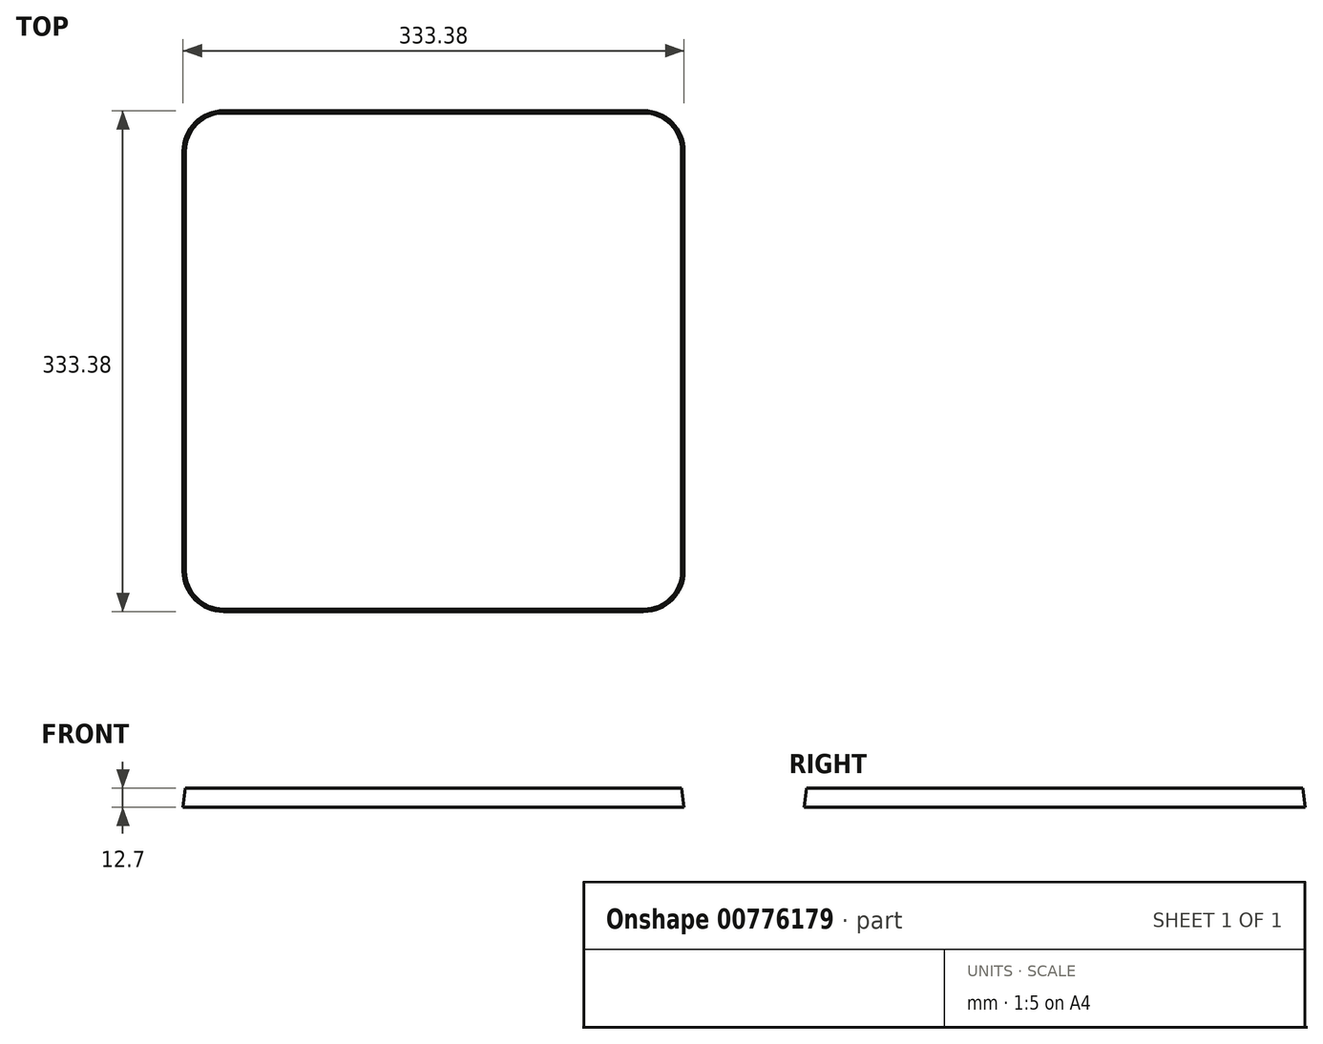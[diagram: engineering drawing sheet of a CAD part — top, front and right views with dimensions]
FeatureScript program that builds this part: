
annotation { "Feature Type Name" : "Feature", "Feature Type Description" : "" }
export const myFeature = defineFeature(function(context is Context, id is Id, definition is map)
    precondition{}
    {
        {
            var Q0;
            Q0=qCreatedBy(makeId("Top.planeOp"),FACE);
            var sketch = newSketch(context, id + "F0", { "sketchPlane" : qUnion([Q0])});
            skLineSegment(sketch, "E0.bottom", {"start": v(139.7, -165.1) * mm, "end": v(-139.7, -165.1) * mm});
            skLineSegment(sketch, "E0.top", {"start": v(139.7, 165.1) * mm, "end": v(-139.7, 165.1) * mm});
            skLineSegment(sketch, "E0.left", {"start": v(165.1, -139.7) * mm, "end": v(165.1, 139.7) * mm});
            skLineSegment(sketch, "E0.right", {"start": v(-165.1, -139.7) * mm, "end": v(-165.1, 139.7) * mm});
            skPoint(sketch, "E0.middle", {"position": v(0, 0) * mm});
            skLineSegment(sketch, "E1.bottom", {"start": v(139.7, -152.4) * mm, "end": v(19.05, -152.4) * mm});
            skLineSegment(sketch, "E1.top", {"start": v(139.7, 152.4) * mm, "end": v(19.05, 152.4) * mm});
            skLineSegment(sketch, "E1.left", {"start": v(152.4, -139.7) * mm, "end": v(152.4, -19.06) * mm});
            skLineSegment(sketch, "E1.right", {"start": v(-152.4, -139.7) * mm, "end": v(-152.4, -19.06) * mm});
            skLineSegment(sketch, "E2.bottom", {"start": v(139.7, -6.36) * mm, "end": v(19.05, -6.36) * mm});
            skLineSegment(sketch, "E2.top", {"start": v(139.7, 6.36) * mm, "end": v(19.05, 6.36) * mm});
            skLineSegment(sketch, "E3.left", {"start": v(6.35, -139.7) * mm, "end": v(6.35, -19.06) * mm});
            skLineSegment(sketch, "E3.right", {"start": v(-6.35, -139.7) * mm, "end": v(-6.35, -19.06) * mm});
            skPoint(sketch, "E4.visualSharp", {"position": v(-165.1, 165.1) * mm});
            skArc(sketch, "E4.filletArc", {"start": v(-139.7, 165.1) * mm, "mid": v(-157.66, 157.66) * mm, "end": v(-165.1, 139.7) * mm});
            skPoint(sketch, "E5.visualSharp", {"position": v(165.1, 165.1) * mm});
            skArc(sketch, "E5.filletArc", {"start": v(165.1, 139.7) * mm, "mid": v(157.66, 157.66) * mm, "end": v(139.7, 165.1) * mm});
            skPoint(sketch, "E6.visualSharp", {"position": v(165.1, -165.1) * mm});
            skArc(sketch, "E6.filletArc", {"start": v(139.7, -165.1) * mm, "mid": v(157.66, -157.66) * mm, "end": v(165.1, -139.7) * mm});
            skPoint(sketch, "E7.visualSharp", {"position": v(-165.1, -165.1) * mm});
            skArc(sketch, "E7.filletArc", {"start": v(-165.1, -139.7) * mm, "mid": v(-157.66, -157.66) * mm, "end": v(-139.7, -165.1) * mm});
            skPoint(sketch, "E8.visualSharp", {"position": v(-152.4, -152.4) * mm});
            skArc(sketch, "E8.filletArc", {"start": v(-152.4, -139.7) * mm, "mid": v(-148.68, -148.68) * mm, "end": v(-139.7, -152.4) * mm});
            skPoint(sketch, "E9.visualSharp", {"position": v(152.4, -152.4) * mm});
            skArc(sketch, "E9.filletArc", {"start": v(139.7, -152.4) * mm, "mid": v(148.68, -148.68) * mm, "end": v(152.4, -139.7) * mm});
            skPoint(sketch, "E10.visualSharp", {"position": v(-152.4, 152.4) * mm});
            skArc(sketch, "E10.filletArc", {"start": v(-139.7, 152.4) * mm, "mid": v(-148.68, 148.68) * mm, "end": v(-152.4, 139.7) * mm});
            skPoint(sketch, "E11.visualSharp", {"position": v(152.4, 152.4) * mm});
            skArc(sketch, "E11.filletArc", {"start": v(152.4, 139.7) * mm, "mid": v(148.68, 148.68) * mm, "end": v(139.7, 152.4) * mm});
            skLineSegment(sketch, "E12.trimOffspring", {"start": v(-6.35, 19.06) * mm, "end": v(-6.35, 139.7) * mm});
            skLineSegment(sketch, "E13.trimOffspring", {"start": v(-19.05, 6.36) * mm, "end": v(-139.7, 6.36) * mm});
            skLineSegment(sketch, "E14.trimOffspring", {"start": v(6.35, 19.06) * mm, "end": v(6.35, 139.7) * mm});
            skLineSegment(sketch, "E15.trimOffspring", {"start": v(-19.05, -6.36) * mm, "end": v(-139.7, -6.36) * mm});
            skLineSegment(sketch, "E16.trimOffspring", {"start": v(-152.4, 19.06) * mm, "end": v(-152.4, 139.7) * mm});
            skLineSegment(sketch, "E17.trimOffspring", {"start": v(-19.05, -152.4) * mm, "end": v(-139.7, -152.4) * mm});
            skLineSegment(sketch, "E18.trimOffspring", {"start": v(152.4, 19.06) * mm, "end": v(152.4, 139.7) * mm});
            skLineSegment(sketch, "E19.trimOffspring", {"start": v(-19.05, 152.4) * mm, "end": v(-139.7, 152.4) * mm});
            skPoint(sketch, "E20.visualSharp", {"position": v(-6.35, 152.4) * mm});
            skArc(sketch, "E20.filletArc", {"start": v(-6.35, 139.7) * mm, "mid": v(-10.06, 148.68) * mm, "end": v(-19.05, 152.4) * mm});
            skPoint(sketch, "E21.visualSharp", {"position": v(6.35, 152.4) * mm});
            skArc(sketch, "E21.filletArc", {"start": v(19.05, 152.4) * mm, "mid": v(10.06, 148.68) * mm, "end": v(6.35, 139.7) * mm});
            skPoint(sketch, "E22.visualSharp", {"position": v(-6.35, 6.36) * mm});
            skArc(sketch, "E22.filletArc", {"start": v(-19.05, 6.36) * mm, "mid": v(-10.06, 10.08) * mm, "end": v(-6.35, 19.06) * mm});
            skPoint(sketch, "E23.visualSharp", {"position": v(-152.4, 6.36) * mm});
            skArc(sketch, "E23.filletArc", {"start": v(-152.4, 19.06) * mm, "mid": v(-148.68, 10.08) * mm, "end": v(-139.7, 6.36) * mm});
            skPoint(sketch, "E24.visualSharp", {"position": v(-152.4, -6.36) * mm});
            skArc(sketch, "E24.filletArc", {"start": v(-139.7, -6.36) * mm, "mid": v(-148.68, -10.08) * mm, "end": v(-152.4, -19.06) * mm});
            skPoint(sketch, "E25.visualSharp", {"position": v(-6.35, -6.36) * mm});
            skArc(sketch, "E25.filletArc", {"start": v(-6.35, -19.06) * mm, "mid": v(-10.06, -10.08) * mm, "end": v(-19.05, -6.36) * mm});
            skPoint(sketch, "E26.visualSharp", {"position": v(6.35, -6.36) * mm});
            skArc(sketch, "E26.filletArc", {"start": v(19.05, -6.36) * mm, "mid": v(10.06, -10.08) * mm, "end": v(6.35, -19.06) * mm});
            skPoint(sketch, "E27.visualSharp", {"position": v(6.35, 6.36) * mm});
            skArc(sketch, "E27.filletArc", {"start": v(6.35, 19.06) * mm, "mid": v(10.06, 10.08) * mm, "end": v(19.05, 6.36) * mm});
            skPoint(sketch, "E28.visualSharp", {"position": v(-6.35, -152.4) * mm});
            skArc(sketch, "E28.filletArc", {"start": v(-19.05, -152.4) * mm, "mid": v(-10.06, -148.68) * mm, "end": v(-6.35, -139.7) * mm});
            skPoint(sketch, "E29.visualSharp", {"position": v(6.35, -152.4) * mm});
            skArc(sketch, "E29.filletArc", {"start": v(6.35, -139.7) * mm, "mid": v(10.06, -148.68) * mm, "end": v(19.05, -152.4) * mm});
            skPoint(sketch, "E30.visualSharp", {"position": v(152.4, -6.36) * mm});
            skArc(sketch, "E30.filletArc", {"start": v(152.4, -19.06) * mm, "mid": v(148.68, -10.08) * mm, "end": v(139.7, -6.36) * mm});
            skPoint(sketch, "E31.visualSharp", {"position": v(152.4, 6.36) * mm});
            skArc(sketch, "E31.filletArc", {"start": v(139.7, 6.36) * mm, "mid": v(148.68, 10.08) * mm, "end": v(152.4, 19.06) * mm});
            skSolve(sketch);
        }
        {
            var Q0;
            Q0=qCreatedBy(makeId("Top.planeOp"),FACE);
            cPlane(context, id + "F1", {"entities" : qUnion([Q0]), "cplaneType" : CPlaneType.OFFSET, "offset" : 190.5 * mm, "width" : 152.4 * mm, "height" : 152.4 * mm});
        }
        {
            var Q0;
            Q0=makeQuery(id+"F0.imprint","IMPRINT",FACE,{"disambiguationData":[TD([[makeQuery(id+"F0.imprint","IMPRINT",EDGE,{"derivedFrom":sQuery(id+"F0.wireOp",EDGE,"E1.bottom")}),-1.0]])]});
            var Q1;
            Q1=makeQuery(id+"F0.imprint","IMPRINT",FACE,{"disambiguationData":[TD([[makeQuery(id+"F0.imprint","IMPRINT",EDGE,{"derivedFrom":sQuery(id+"F0.wireOp",EDGE,"E1.top")}),1.0]])]});
            var Q2;
            Q2=makeQuery(id+"F0.imprint","IMPRINT",FACE,{"disambiguationData":[TD([[makeQuery(id+"F0.imprint","IMPRINT",EDGE,{"derivedFrom":sQuery(id+"F0.wireOp",EDGE,"E1.right")}),-1.0]])]});
            var Q3;
            Q3=makeQuery(id+"F0.imprint","IMPRINT",FACE,{"disambiguationData":[TD([[makeQuery(id+"F0.imprint","IMPRINT",EDGE,{"derivedFrom":sQuery(id+"F0.wireOp",EDGE,"E10.filletArc")}),1.0]])]});
            var Q4;
            Q4=makeQuery(id+"F0.imprint","IMPRINT",FACE,{"disambiguationData":[TD([[makeQuery(id+"F0.imprint","IMPRINT",EDGE,{"derivedFrom":sQuery(id+"F0.wireOp",EDGE,"E0.bottom")}),-1.0]])]});
            extrude(context, id + "F2", {"entities" : qUnion([Q0, Q1, Q2, Q3, Q4]), "oppositeDirection" : true, "depth" : 12.7 * mm, "offsetDistance" : 25.4 * mm, "hasDraft" : true, "draftAngle" : 7.12 * degree});
        }
    });
